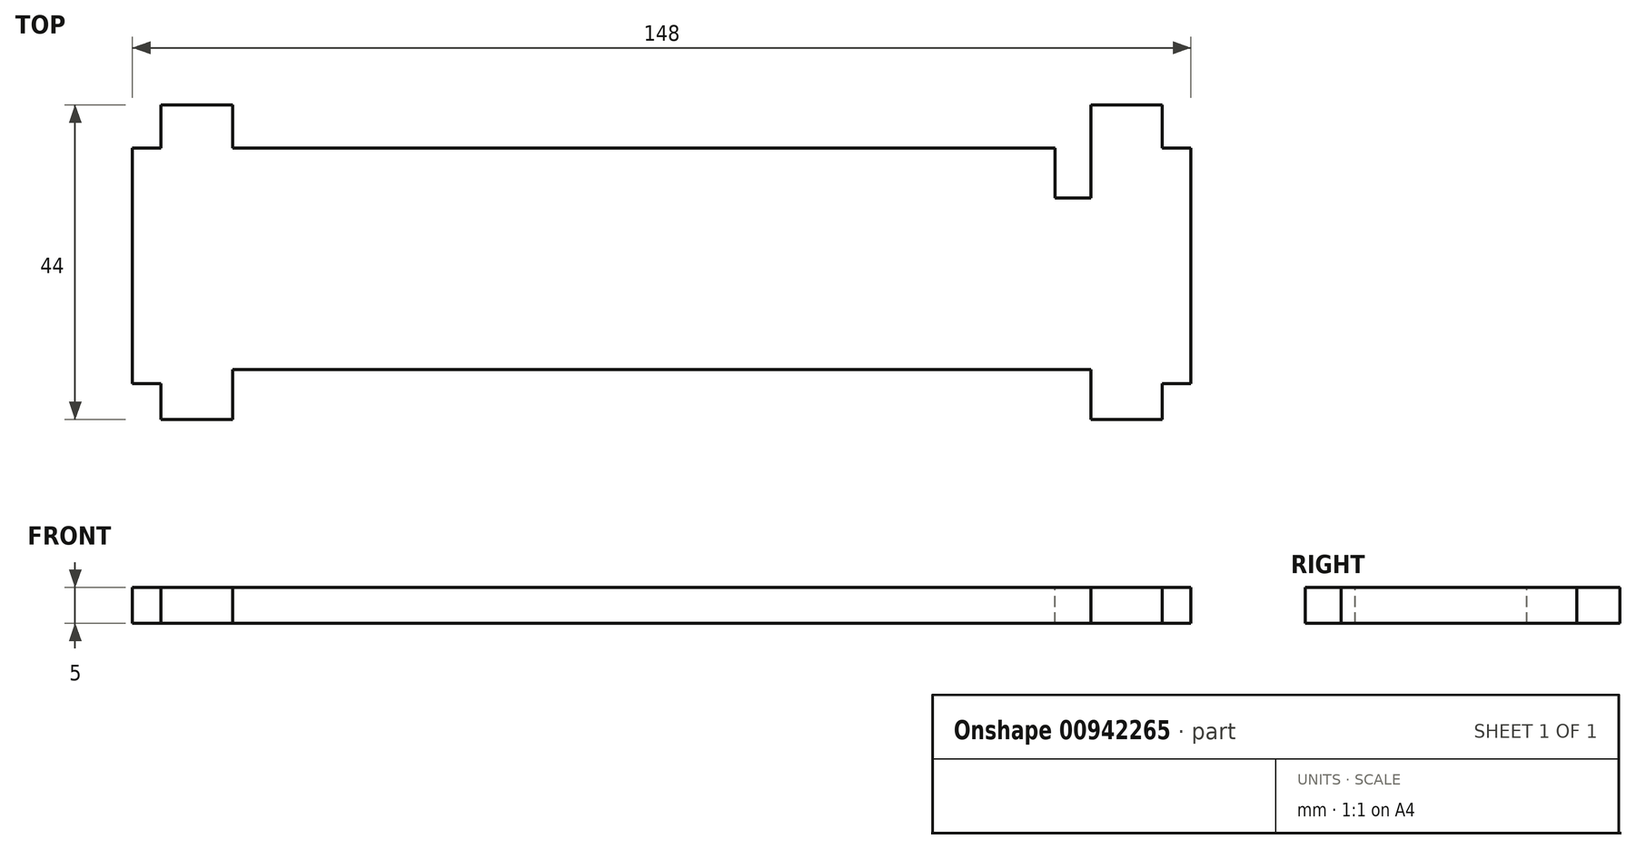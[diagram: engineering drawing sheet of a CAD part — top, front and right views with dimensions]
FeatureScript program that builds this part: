
annotation { "Feature Type Name" : "Feature", "Feature Type Description" : "" }
export const myFeature = defineFeature(function(context is Context, id is Id, definition is map)
    precondition{}
    {
        {
            var Q0;
            Q0=qCreatedBy(makeId("Top.planeOp"),FACE);
            var sketch = newSketch(context, id + "F0", { "sketchPlane" : qUnion([Q0])});
            skLineSegment(sketch, "E0.bottom", {"start": v(-70, -15) * mm, "end": v(70, -15) * mm});
            skLineSegment(sketch, "E0.top", {"start": v(-70, 15) * mm, "end": v(70, 15) * mm});
            skLineSegment(sketch, "E0.left", {"start": v(-70, -15) * mm, "end": v(-70, 15) * mm});
            skLineSegment(sketch, "E0.right", {"start": v(70, -15) * mm, "end": v(70, 15) * mm});
            skSolve(sketch);
        }
        {
            var Q0;
            Q0=makeQuery(id+"F0.imprint","IMPRINT",FACE,{"disambiguationData":[TD([[makeQuery(id+"F0.imprint","IMPRINT",EDGE,{"derivedFrom":sQuery(id+"F0.wireOp",EDGE,"E0.bottom")}),1.0]])]});
            extrude(context, id + "F1", {"entities" : qUnion([Q0]), "depth" : 5 * mm, "offsetDistance" : 25 * mm});
        }
        {
            var Q0;
            Q0=makeQuery(id+"F1.opExtrude","CAP_FACE",FACE,{"disambiguationData":[OSD([sQuery(id+"F0.wireOp",EDGE,"E0.bottom"),sQuery(id+"F0.wireOp",EDGE,"E0.top"),sQuery(id+"F0.wireOp",EDGE,"E0.left"),sQuery(id+"F0.wireOp",EDGE,"E0.right")])],"isStart":false});
            var sketch = newSketch(context, id + "F2", { "sketchPlane" : qUnion([Q0])});
            skLineSegment(sketch, "E1.bottom", {"start": v(-70, 15) * mm, "end": v(-60, 15) * mm});
            skLineSegment(sketch, "E1.top", {"start": v(-70, 20) * mm, "end": v(-60, 20) * mm});
            skLineSegment(sketch, "E1.left", {"start": v(-70, 15) * mm, "end": v(-70, 20) * mm});
            skLineSegment(sketch, "E1.right", {"start": v(-60, 15) * mm, "end": v(-60, 20) * mm});
            skLineSegment(sketch, "E2.bottom", {"start": v(60, 15) * mm, "end": v(70, 15) * mm});
            skLineSegment(sketch, "E2.top", {"start": v(60, 20) * mm, "end": v(70, 20) * mm});
            skLineSegment(sketch, "E2.left", {"start": v(60, 15) * mm, "end": v(60, 20) * mm});
            skLineSegment(sketch, "E2.right", {"start": v(70, 15) * mm, "end": v(70, 20) * mm});
            skLineSegment(sketch, "E3.bottom", {"start": v(-70, -24) * mm, "end": v(-60, -24) * mm});
            skLineSegment(sketch, "E3.top", {"start": v(-70, -15) * mm, "end": v(-60, -15) * mm});
            skLineSegment(sketch, "E3.left", {"start": v(-70, -24) * mm, "end": v(-70, -15) * mm});
            skLineSegment(sketch, "E3.right", {"start": v(-60, -24) * mm, "end": v(-60, -15) * mm});
            skLineSegment(sketch, "E4.bottom", {"start": v(60, -24) * mm, "end": v(70, -24) * mm});
            skLineSegment(sketch, "E4.top", {"start": v(60, -15) * mm, "end": v(70, -15) * mm});
            skLineSegment(sketch, "E4.left", {"start": v(60, -24) * mm, "end": v(60, -15) * mm});
            skLineSegment(sketch, "E4.right", {"start": v(70, -24) * mm, "end": v(70, -15) * mm});
            skSolve(sketch);
        }
        {
            var Q0;
            Q0=makeQuery(id+"F2.imprint","IMPRINT",FACE,{"disambiguationData":[TD([[makeQuery(id+"F2.imprint","IMPRINT",EDGE,{"derivedFrom":sQuery(id+"F2.wireOp",EDGE,"E2.bottom")}),1.0]])]});
            var Q1;
            Q1=makeQuery(id+"F2.imprint","IMPRINT",FACE,{"disambiguationData":[TD([[makeQuery(id+"F2.imprint","IMPRINT",EDGE,{"derivedFrom":sQuery(id+"F2.wireOp",EDGE,"E1.bottom")}),1.0]])]});
            var Q2;
            Q2=makeQuery(id+"F2.imprint","IMPRINT",FACE,{"disambiguationData":[TD([[makeQuery(id+"F2.imprint","IMPRINT",EDGE,{"derivedFrom":sQuery(id+"F2.wireOp",EDGE,"E3.bottom")}),1.0]])]});
            var Q3;
            Q3=makeQuery(id+"F2.imprint","IMPRINT",FACE,{"disambiguationData":[TD([[makeQuery(id+"F2.imprint","IMPRINT",EDGE,{"derivedFrom":sQuery(id+"F2.wireOp",EDGE,"E4.bottom")}),1.0]])]});
            extrude(context, id + "F3", {"entities" : qUnion([Q0, Q1, Q2, Q3]), "oppositeDirection" : true, "depth" : 5 * mm, "offsetDistance" : 25 * mm});
        }
        {
            var Q0;
            Q0=makeQuery(id+"F3.opExtrude","SWEPT_BODY",BODY,{"disambiguationData":[OSD([sQuery(id+"F2.wireOp",EDGE,"E1.bottom"),sQuery(id+"F2.wireOp",EDGE,"E1.top"),sQuery(id+"F2.wireOp",EDGE,"E1.left"),sQuery(id+"F2.wireOp",EDGE,"E1.right")])]});
            var Q1;
            Q1=makeQuery(id+"F3.opExtrude","SWEPT_BODY",BODY,{"disambiguationData":[OSD([sQuery(id+"F2.wireOp",EDGE,"E2.bottom"),sQuery(id+"F2.wireOp",EDGE,"E2.top"),sQuery(id+"F2.wireOp",EDGE,"E2.left"),sQuery(id+"F2.wireOp",EDGE,"E2.right")])]});
            var Q2;
            Q2=makeQuery(id+"F3.opExtrude","SWEPT_BODY",BODY,{"disambiguationData":[OSD([sQuery(id+"F2.wireOp",EDGE,"E3.bottom"),sQuery(id+"F2.wireOp",EDGE,"E3.top"),sQuery(id+"F2.wireOp",EDGE,"E3.left"),sQuery(id+"F2.wireOp",EDGE,"E3.right")])]});
            var Q3;
            Q3=makeQuery(id+"F3.opExtrude","SWEPT_BODY",BODY,{"disambiguationData":[OSD([sQuery(id+"F2.wireOp",EDGE,"E4.bottom"),sQuery(id+"F2.wireOp",EDGE,"E4.top"),sQuery(id+"F2.wireOp",EDGE,"E4.left"),sQuery(id+"F2.wireOp",EDGE,"E4.right")])]});
            var Q4;
            Q4=makeQuery(id+"F1.opExtrude","SWEPT_BODY",BODY,{"disambiguationData":[OSD([sQuery(id+"F0.wireOp",EDGE,"E0.bottom"),sQuery(id+"F0.wireOp",EDGE,"E0.top"),sQuery(id+"F0.wireOp",EDGE,"E0.left"),sQuery(id+"F0.wireOp",EDGE,"E0.right")])]});
            booleanBodies(context, id + "F4", {"operationType" : BooleanOperationType.UNION, "tools" : qUnion([Q0, Q1, Q2, Q3, Q4])});
        }
        {
            var Q0;
            Q0=makeQuery(id+"F4.opBoolean","MERGE",FACE,{"derivedFrom":[makeQuery(id+"F1.opExtrude","CAP_FACE",FACE,{"disambiguationData":[OSD([sQuery(id+"F0.wireOp",EDGE,"E0.bottom"),sQuery(id+"F0.wireOp",EDGE,"E0.top"),sQuery(id+"F0.wireOp",EDGE,"E0.left"),sQuery(id+"F0.wireOp",EDGE,"E0.right")])],"isStart":false}),makeQuery(id+"F3.opExtrude","CAP_FACE",FACE,{"disambiguationData":[OSD([sQuery(id+"F2.wireOp",EDGE,"E1.bottom"),sQuery(id+"F2.wireOp",EDGE,"E1.top"),sQuery(id+"F2.wireOp",EDGE,"E1.left"),sQuery(id+"F2.wireOp",EDGE,"E1.right")])],"isStart":true}),makeQuery(id+"F3.opExtrude","CAP_FACE",FACE,{"disambiguationData":[OSD([sQuery(id+"F2.wireOp",EDGE,"E2.bottom"),sQuery(id+"F2.wireOp",EDGE,"E2.top"),sQuery(id+"F2.wireOp",EDGE,"E2.left"),sQuery(id+"F2.wireOp",EDGE,"E2.right")])],"isStart":true}),makeQuery(id+"F3.opExtrude","CAP_FACE",FACE,{"disambiguationData":[OSD([sQuery(id+"F2.wireOp",EDGE,"E3.bottom"),sQuery(id+"F2.wireOp",EDGE,"E3.top"),sQuery(id+"F2.wireOp",EDGE,"E3.left"),sQuery(id+"F2.wireOp",EDGE,"E3.right")])],"isStart":true}),makeQuery(id+"F3.opExtrude","CAP_FACE",FACE,{"disambiguationData":[OSD([sQuery(id+"F2.wireOp",EDGE,"E4.bottom"),sQuery(id+"F2.wireOp",EDGE,"E4.top"),sQuery(id+"F2.wireOp",EDGE,"E4.left"),sQuery(id+"F2.wireOp",EDGE,"E4.right")])],"isStart":true})]});
            var sketch = newSketch(context, id + "F5", { "sketchPlane" : qUnion([Q0])});
            skLineSegment(sketch, "E5.bottom", {"start": v(55, 7) * mm, "end": v(60, 7) * mm});
            skLineSegment(sketch, "E5.top", {"start": v(55, 15) * mm, "end": v(60, 15) * mm});
            skLineSegment(sketch, "E5.left", {"start": v(55, 7) * mm, "end": v(55, 15) * mm});
            skLineSegment(sketch, "E5.right", {"start": v(60, 7) * mm, "end": v(60, 15) * mm});
            skSolve(sketch);
        }
        {
            var Q0;
            Q0=makeQuery(id+"F5.imprint","IMPRINT",FACE,{"disambiguationData":[TD([[makeQuery(id+"F5.imprint","IMPRINT",EDGE,{"derivedFrom":sQuery(id+"F5.wireOp",EDGE,"RuR1eCBN-IUNf-TQCT-UWBD-UVoxSlnhnZJr.bottom")}),1.0]])]});
            var Q1;
            Q1=makeQuery(id+"F5.imprint","IMPRINT",FACE,{"disambiguationData":[TD([[makeQuery(id+"F5.imprint","IMPRINT",EDGE,{"derivedFrom":sQuery(id+"F5.wireOp",EDGE,"E5.bottom")}),1.0]])]});
            extrude(context, id + "F6", {"entities" : qUnion([Q0, Q1]), "operationType" : NewBodyOperationType.REMOVE, "oppositeDirection" : true, "depth" : 25 * mm, "offsetDistance" : 25 * mm});
        }
        {
            var Q0;
            Q0=makeQuery(id+"F4.opBoolean","MERGE",FACE,{"derivedFrom":[makeQuery(id+"F1.opExtrude","CAP_FACE",FACE,{"disambiguationData":[OSD([sQuery(id+"F0.wireOp",EDGE,"E0.bottom"),sQuery(id+"F0.wireOp",EDGE,"E0.top"),sQuery(id+"F0.wireOp",EDGE,"E0.left"),sQuery(id+"F0.wireOp",EDGE,"E0.right")])],"isStart":false}),makeQuery(id+"F3.opExtrude","CAP_FACE",FACE,{"disambiguationData":[OSD([sQuery(id+"F2.wireOp",EDGE,"E1.bottom"),sQuery(id+"F2.wireOp",EDGE,"E1.top"),sQuery(id+"F2.wireOp",EDGE,"E1.left"),sQuery(id+"F2.wireOp",EDGE,"E1.right")])],"isStart":true}),makeQuery(id+"F3.opExtrude","CAP_FACE",FACE,{"disambiguationData":[OSD([sQuery(id+"F2.wireOp",EDGE,"E2.bottom"),sQuery(id+"F2.wireOp",EDGE,"E2.top"),sQuery(id+"F2.wireOp",EDGE,"E2.left"),sQuery(id+"F2.wireOp",EDGE,"E2.right")])],"isStart":true}),makeQuery(id+"F3.opExtrude","CAP_FACE",FACE,{"disambiguationData":[OSD([sQuery(id+"F2.wireOp",EDGE,"E3.bottom"),sQuery(id+"F2.wireOp",EDGE,"E3.top"),sQuery(id+"F2.wireOp",EDGE,"E3.left"),sQuery(id+"F2.wireOp",EDGE,"E3.right")])],"isStart":true}),makeQuery(id+"F3.opExtrude","CAP_FACE",FACE,{"disambiguationData":[OSD([sQuery(id+"F2.wireOp",EDGE,"E4.bottom"),sQuery(id+"F2.wireOp",EDGE,"E4.top"),sQuery(id+"F2.wireOp",EDGE,"E4.left"),sQuery(id+"F2.wireOp",EDGE,"E4.right")])],"isStart":true})]});
            var sketch = newSketch(context, id + "F7", { "sketchPlane" : qUnion([Q0])});
            skLineSegment(sketch, "E6.bottom", {"start": v(-60, -15) * mm, "end": v(60, -15) * mm});
            skLineSegment(sketch, "E6.top", {"start": v(-60, -17) * mm, "end": v(60, -17) * mm});
            skLineSegment(sketch, "E6.left", {"start": v(-60, -15) * mm, "end": v(-60, -17) * mm});
            skLineSegment(sketch, "E6.right", {"start": v(60, -15) * mm, "end": v(60, -17) * mm});
            skSolve(sketch);
        }
        {
            var Q0;
            Q0=makeQuery(id+"F7.imprint","IMPRINT",FACE,{"disambiguationData":[TD([[makeQuery(id+"F7.imprint","IMPRINT",EDGE,{"derivedFrom":sQuery(id+"F7.wireOp",EDGE,"E6.bottom")}),-1.0]])]});
            extrude(context, id + "F8", {"entities" : qUnion([Q0]), "operationType" : NewBodyOperationType.ADD, "oppositeDirection" : true, "depth" : 5 * mm, "offsetDistance" : 25 * mm});
        }
        {
            var Q0;
            Q0=makeQuery(id+"F12.boolean.opBoolean","MERGE",FACE,{"derivedFrom":[makeQuery(id+"F8.boolean.opBoolean","MERGE",FACE,{"derivedFrom":[makeQuery(id+"F4.opBoolean","MERGE",FACE,{"derivedFrom":[makeQuery(id+"F1.opExtrude","CAP_FACE",FACE,{"disambiguationData":[OSD([sQuery(id+"F0.wireOp",EDGE,"E0.bottom"),sQuery(id+"F0.wireOp",EDGE,"E0.top"),sQuery(id+"F0.wireOp",EDGE,"E0.left"),sQuery(id+"F0.wireOp",EDGE,"E0.right")])],"isStart":false}),makeQuery(id+"F3.opExtrude","CAP_FACE",FACE,{"disambiguationData":[OSD([sQuery(id+"F2.wireOp",EDGE,"E1.bottom"),sQuery(id+"F2.wireOp",EDGE,"E1.top"),sQuery(id+"F2.wireOp",EDGE,"E1.left"),sQuery(id+"F2.wireOp",EDGE,"E1.right")])],"isStart":true}),makeQuery(id+"F3.opExtrude","CAP_FACE",FACE,{"disambiguationData":[OSD([sQuery(id+"F2.wireOp",EDGE,"E2.bottom"),sQuery(id+"F2.wireOp",EDGE,"E2.top"),sQuery(id+"F2.wireOp",EDGE,"E2.left"),sQuery(id+"F2.wireOp",EDGE,"E2.right")])],"isStart":true}),makeQuery(id+"F3.opExtrude","CAP_FACE",FACE,{"disambiguationData":[OSD([sQuery(id+"F2.wireOp",EDGE,"E3.bottom"),sQuery(id+"F2.wireOp",EDGE,"E3.top"),sQuery(id+"F2.wireOp",EDGE,"E3.left"),sQuery(id+"F2.wireOp",EDGE,"E3.right")])],"isStart":true}),makeQuery(id+"F3.opExtrude","CAP_FACE",FACE,{"disambiguationData":[OSD([sQuery(id+"F2.wireOp",EDGE,"E4.bottom"),sQuery(id+"F2.wireOp",EDGE,"E4.top"),sQuery(id+"F2.wireOp",EDGE,"E4.left"),sQuery(id+"F2.wireOp",EDGE,"E4.right")])],"isStart":true})]}),makeQuery(id+"F8.opExtrude","CAP_FACE",FACE,{"disambiguationData":[OSD([sQuery(id+"F7.wireOp",EDGE,"E6.bottom"),sQuery(id+"F7.wireOp",EDGE,"E6.top"),sQuery(id+"F7.wireOp",EDGE,"E6.left"),sQuery(id+"F7.wireOp",EDGE,"E6.right")])],"isStart":true})]}),makeQuery(id+"F12.opExtrude","CAP_FACE",FACE,{"disambiguationData":[OSD([sQuery(id+"F11.wireOp",EDGE,"E8.bottom"),sQuery(id+"F11.wireOp",EDGE,"E8.top"),sQuery(id+"F11.wireOp",EDGE,"E8.left"),sQuery(id+"F11.wireOp",EDGE,"E8.right")])],"isStart":false}),makeQuery(id+"F12.opExtrude","CAP_FACE",FACE,{"disambiguationData":[OSD([sQuery(id+"F11.wireOp",EDGE,"E9.bottom"),sQuery(id+"F11.wireOp",EDGE,"E9.top"),sQuery(id+"F11.wireOp",EDGE,"E9.left"),sQuery(id+"F11.wireOp",EDGE,"E9.right")])],"isStart":false})]});
            var sketch = newSketch(context, id + "F9", { "sketchPlane" : qUnion([Q0])});
            skLineSegment(sketch, "E7.bottom", {"start": v(-60, 15) * mm, "end": v(55, 15) * mm});
            skLineSegment(sketch, "E7.top", {"start": v(-60, 14) * mm, "end": v(55, 14) * mm});
            skLineSegment(sketch, "E7.left", {"start": v(-60, 15) * mm, "end": v(-60, 14) * mm});
            skLineSegment(sketch, "E7.right", {"start": v(55, 15) * mm, "end": v(55, 14) * mm});
            skSolve(sketch);
        }
        {
            var Q0;
            Q0=makeQuery(id+"F9.imprint","IMPRINT",FACE,{"disambiguationData":[TD([[makeQuery(id+"F9.imprint","IMPRINT",EDGE,{"derivedFrom":sQuery(id+"F9.wireOp",EDGE,"E7.bottom")}),-1.0]])]});
            extrude(context, id + "F10", {"entities" : qUnion([Q0]), "operationType" : NewBodyOperationType.REMOVE, "oppositeDirection" : true, "depth" : 25 * mm, "offsetDistance" : 25 * mm});
        }
        {
            var Q0;
            Q0=qCreatedBy(makeId("Top.planeOp"),FACE);
            var sketch = newSketch(context, id + "F11", { "sketchPlane" : qUnion([Q0])});
            skLineSegment(sketch, "E8.bottom", {"start": v(-70, -19) * mm, "end": v(-74, -19) * mm});
            skLineSegment(sketch, "E8.top", {"start": v(-70, 14) * mm, "end": v(-74, 14) * mm});
            skLineSegment(sketch, "E8.left", {"start": v(-70, -19) * mm, "end": v(-70, 14) * mm});
            skLineSegment(sketch, "E8.right", {"start": v(-74, -19) * mm, "end": v(-74, 14) * mm});
            skPoint(sketch, "E8.middle", {"position": v(-72, 0) * mm});
            skLineSegment(sketch, "E9.bottom", {"start": v(74, -19) * mm, "end": v(70, -19) * mm});
            skLineSegment(sketch, "E9.top", {"start": v(74, 14) * mm, "end": v(70, 14) * mm});
            skLineSegment(sketch, "E9.left", {"start": v(74, -19) * mm, "end": v(74, 14) * mm});
            skLineSegment(sketch, "E9.right", {"start": v(70, -19) * mm, "end": v(70, 14) * mm});
            skPoint(sketch, "E9.middle", {"position": v(72, 0) * mm});
            skSolve(sketch);
        }
        {
            var Q0;
            Q0=makeQuery(id+"F11.imprint","IMPRINT",FACE,{"disambiguationData":[TD([[makeQuery(id+"F11.imprint","IMPRINT",EDGE,{"derivedFrom":sQuery(id+"F11.wireOp",EDGE,"E8.bottom")}),-1.0]])]});
            var Q1;
            Q1=makeQuery(id+"F11.imprint","IMPRINT",FACE,{"disambiguationData":[TD([[makeQuery(id+"F11.imprint","IMPRINT",EDGE,{"derivedFrom":sQuery(id+"F11.wireOp",EDGE,"E9.bottom")}),-1.0]])]});
            extrude(context, id + "F12", {"entities" : qUnion([Q0, Q1]), "operationType" : NewBodyOperationType.ADD, "depth" : 5 * mm, "offsetDistance" : 25 * mm});
        }
    });
